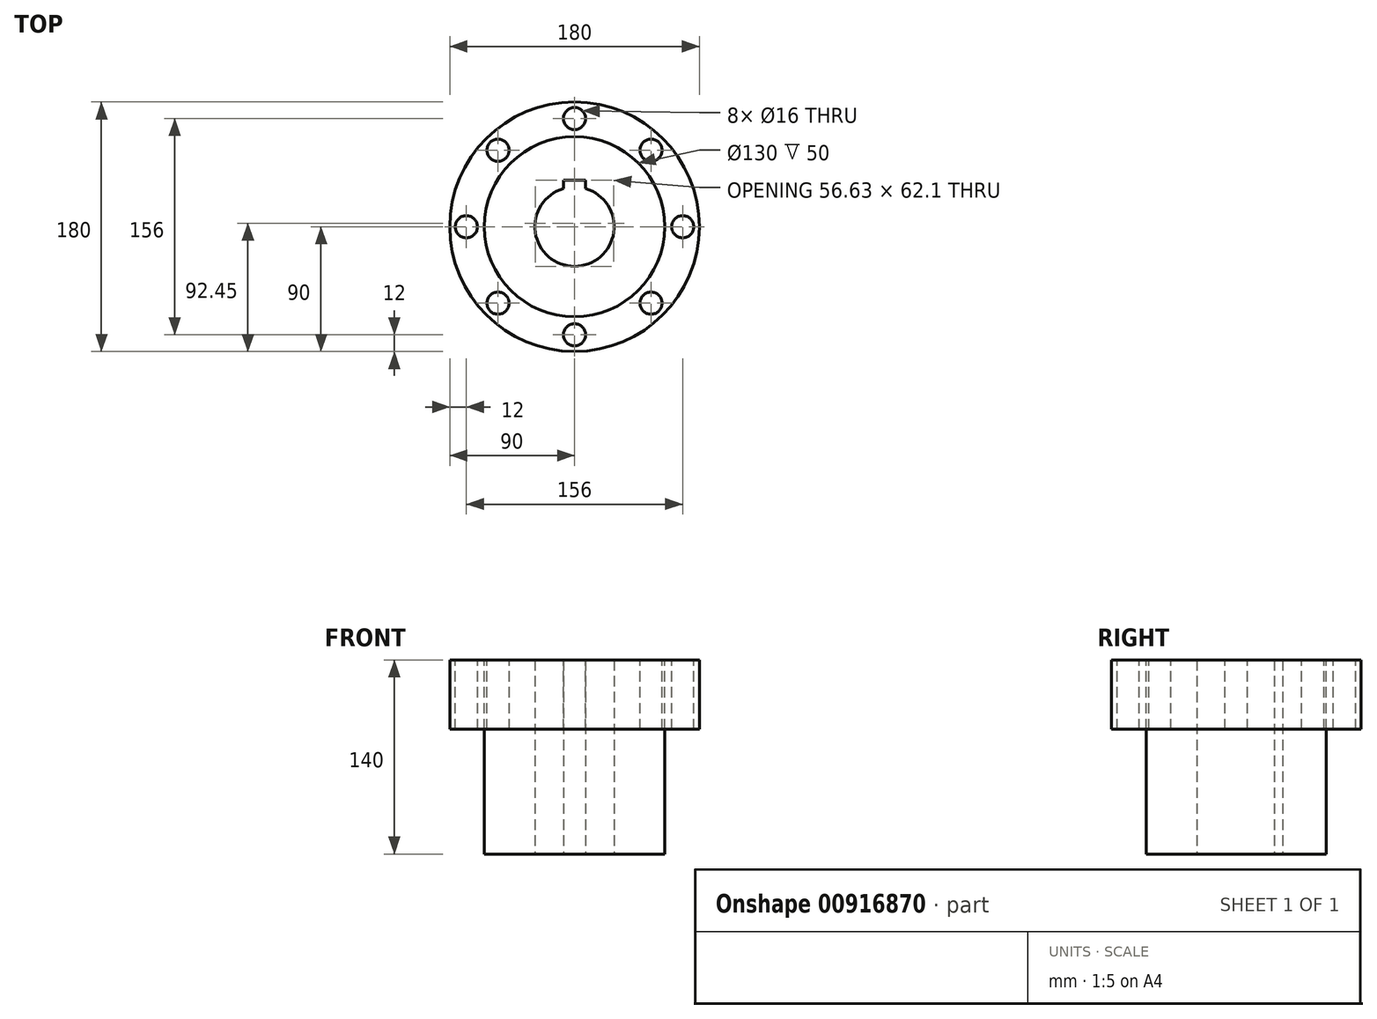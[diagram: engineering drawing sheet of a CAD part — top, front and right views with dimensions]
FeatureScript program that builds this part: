
annotation { "Feature Type Name" : "Feature", "Feature Type Description" : "" }
export const myFeature = defineFeature(function(context is Context, id is Id, definition is map)
    precondition{}
    {
        {
            var Q0;
            Q0=qCreatedBy(makeId("Top.planeOp"),FACE);
            var sketch = newSketch(context, id + "F0", { "sketchPlane" : qUnion([Q0])});
            skCircle(sketch, "E0", {"center": v(0, 0) * mm, "radius": 65 * mm});
            skArc(sketch, "E1", {"start": v(-8, 27.46) * mm, "mid": v(0, -28.6) * mm, "end": v(8, 27.46) * mm});
            skLineSegment(sketch, "E2", {"start": v(-8, 33.5) * mm, "end": v(-8, 27.46) * mm});
            skLineSegment(sketch, "E3", {"start": v(-8, 33.5) * mm, "end": v(8, 33.5) * mm});
            skLineSegment(sketch, "E4", {"start": v(8, 27.46) * mm, "end": v(8, 33.5) * mm});
            skSolve(sketch);
        }
        {
            var Q0;
            Q0=makeQuery(id+"F0.imprint","IMPRINT",FACE,{"disambiguationData":[TD([[makeQuery(id+"F0.imprint","IMPRINT",EDGE,{"derivedFrom":sQuery(id+"F0.wireOp",EDGE,"E0")}),1.0]])]});
            extrude(context, id + "F1", {"entities" : qUnion([Q0]), "depth" : 140 * mm, "offsetDistance" : 25 * mm});
        }
        {
            var Q0;
            Q0=makeQuery(id+"F1.opExtrude","CAP_FACE",FACE,{"disambiguationData":[OSD([sQuery(id+"F0.wireOp",EDGE,"E0"),sQuery(id+"F0.wireOp",EDGE,"E1"),sQuery(id+"F0.wireOp",EDGE,"E2"),sQuery(id+"F0.wireOp",EDGE,"E3"),sQuery(id+"F0.wireOp",EDGE,"E4")])],"isStart":false});
            var sketch = newSketch(context, id + "F2", { "sketchPlane" : qUnion([Q0])});
            skCircle(sketch, "E5", {"center": v(0, 0) * mm, "radius": 90 * mm});
            skCircle(sketch, "E6", {"center": v(0, 0) * mm, "radius": 55 * mm});
            skSolve(sketch);
        }
        {
            var Q0;
            Q0=makeQuery(id+"F2.imprint","IMPRINT",FACE,{"disambiguationData":[TD([[makeQuery(id+"F2.imprint","IMPRINT",EDGE,{"derivedFrom":sQuery(id+"F2.wireOp",EDGE,"E5")}),1.0]])]});
            extrude(context, id + "F3", {"entities" : qUnion([Q0]), "oppositeDirection" : true, "depth" : 50 * mm, "offsetDistance" : 25 * mm});
        }
        {
            var Q0;
            Q0=makeQuery(id+"F3.opExtrude","CAP_FACE",FACE,{"disambiguationData":[OSD([sQuery(id+"F0.wireOp",EDGE,"E0"),sQuery(id+"F2.wireOp",EDGE,"E5")])],"isStart":true});
            var sketch = newSketch(context, id + "F4", { "sketchPlane" : qUnion([Q0])});
            skCircle(sketch, "E7", {"center": v(0, 78) * mm, "radius": 8 * mm});
            skCircle(sketch, "E8.1.0", {"center": v(-55.15, 55.15) * mm, "radius": 8 * mm});
            skCircle(sketch, "E8.2.0", {"center": v(-78, 0) * mm, "radius": 8 * mm});
            skCircle(sketch, "E8.3.0", {"center": v(-55.15, -55.15) * mm, "radius": 8 * mm});
            skCircle(sketch, "E8.4.0", {"center": v(0, -78) * mm, "radius": 8 * mm});
            skCircle(sketch, "E8.5.0", {"center": v(55.15, -55.15) * mm, "radius": 8 * mm});
            skCircle(sketch, "E8.6.0", {"center": v(78, 0) * mm, "radius": 8 * mm});
            skCircle(sketch, "E8.7.0", {"center": v(55.15, 55.15) * mm, "radius": 8 * mm});
            skPoint(sketch, "E8.center", {"position": v(0, 0) * mm});
            skSolve(sketch);
        }
        {
            var Q0;
            Q0=makeQuery(id+"F4.imprint","IMPRINT",FACE,{"disambiguationData":[TD([[makeQuery(id+"F4.imprint","IMPRINT",EDGE,{"derivedFrom":sQuery(id+"F4.wireOp",EDGE,"E8.1.0")}),1.0]])]});
            var Q1;
            Q1=makeQuery(id+"F4.imprint","IMPRINT",FACE,{"disambiguationData":[TD([[makeQuery(id+"F4.imprint","IMPRINT",EDGE,{"derivedFrom":sQuery(id+"F4.wireOp",EDGE,"E7")}),1.0]])]});
            var Q2;
            Q2=makeQuery(id+"F4.imprint","IMPRINT",FACE,{"disambiguationData":[TD([[makeQuery(id+"F4.imprint","IMPRINT",EDGE,{"derivedFrom":sQuery(id+"F4.wireOp",EDGE,"E8.7.0")}),1.0]])]});
            var Q3;
            Q3=makeQuery(id+"F4.imprint","IMPRINT",FACE,{"disambiguationData":[TD([[makeQuery(id+"F4.imprint","IMPRINT",EDGE,{"derivedFrom":sQuery(id+"F4.wireOp",EDGE,"E8.6.0")}),1.0]])]});
            var Q4;
            Q4=makeQuery(id+"F4.imprint","IMPRINT",FACE,{"disambiguationData":[TD([[makeQuery(id+"F4.imprint","IMPRINT",EDGE,{"derivedFrom":sQuery(id+"F4.wireOp",EDGE,"E8.5.0")}),1.0]])]});
            var Q5;
            Q5=makeQuery(id+"F4.imprint","IMPRINT",FACE,{"disambiguationData":[TD([[makeQuery(id+"F4.imprint","IMPRINT",EDGE,{"derivedFrom":sQuery(id+"F4.wireOp",EDGE,"E8.4.0")}),1.0]])]});
            var Q6;
            Q6=makeQuery(id+"F4.imprint","IMPRINT",FACE,{"disambiguationData":[TD([[makeQuery(id+"F4.imprint","IMPRINT",EDGE,{"derivedFrom":sQuery(id+"F4.wireOp",EDGE,"E8.3.0")}),1.0]])]});
            var Q7;
            Q7=makeQuery(id+"F4.imprint","IMPRINT",FACE,{"disambiguationData":[TD([[makeQuery(id+"F4.imprint","IMPRINT",EDGE,{"derivedFrom":sQuery(id+"F4.wireOp",EDGE,"E8.2.0")}),1.0]])]});
            extrude(context, id + "F5", {"entities" : qUnion([Q0, Q1, Q2, Q3, Q4, Q5, Q6, Q7]), "operationType" : NewBodyOperationType.REMOVE, "oppositeDirection" : true, "depth" : 100 * mm, "offsetDistance" : 25 * mm});
        }
    });
